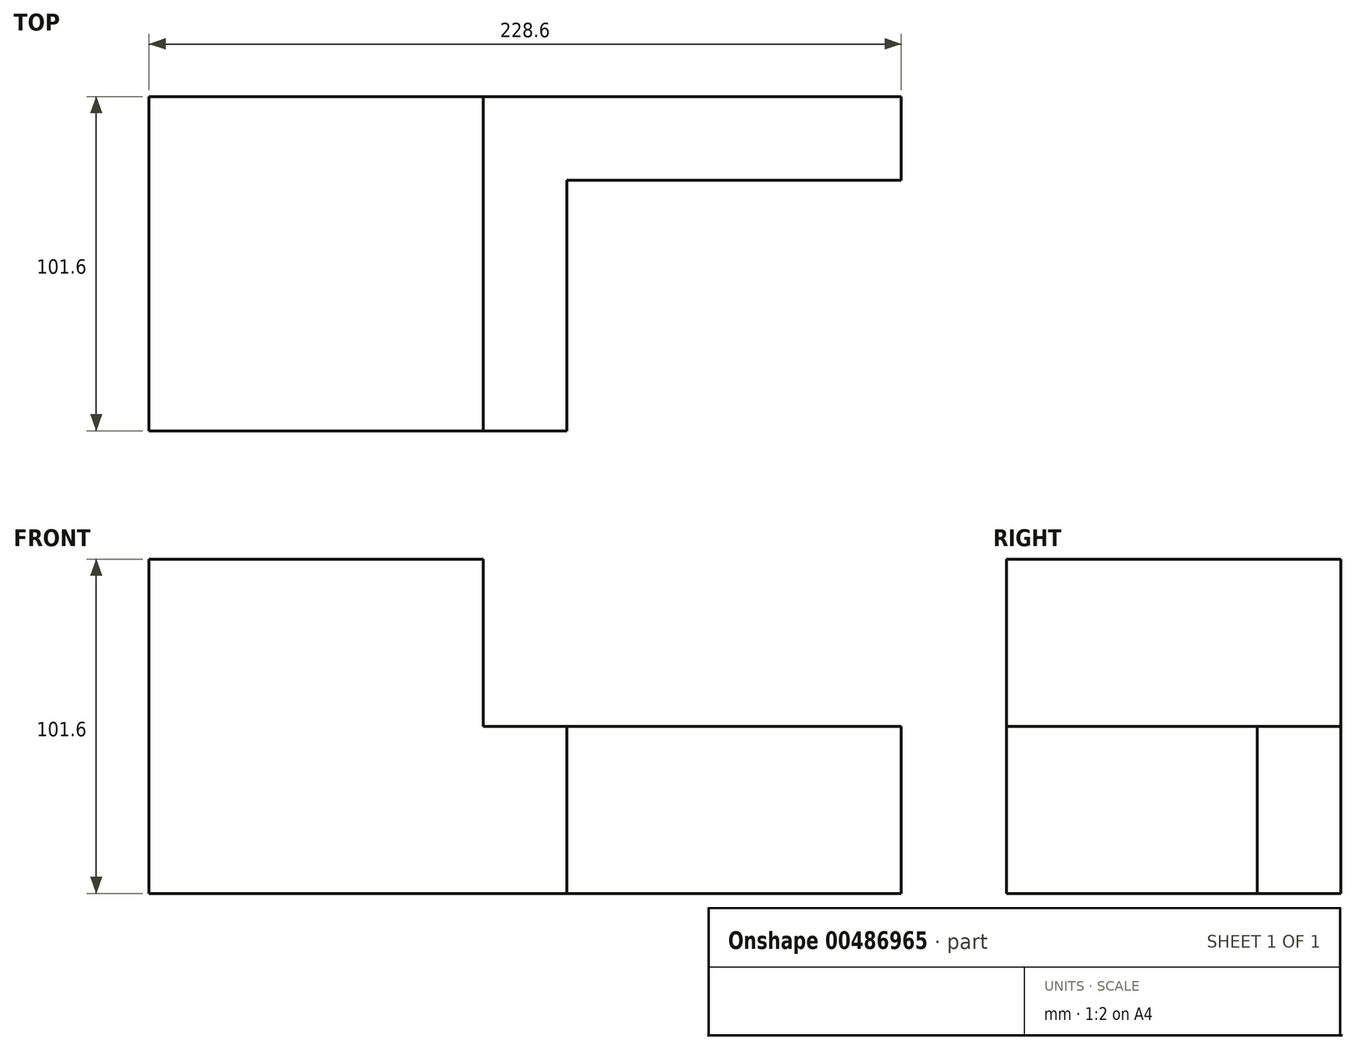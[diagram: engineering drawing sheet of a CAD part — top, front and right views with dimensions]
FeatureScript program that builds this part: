
annotation { "Feature Type Name" : "Feature", "Feature Type Description" : "" }
export const myFeature = defineFeature(function(context is Context, id is Id, definition is map)
    precondition{}
    {
        {
            var Q0;
            Q0=qCreatedBy(makeId("Front.planeOp"),FACE);
            var sketch = newSketch(context, id + "F0", { "sketchPlane" : qUnion([Q0])});
            skLineSegment(sketch, "E0.bottom", {"start": v(0, 0) * mm, "end": v(127, 0) * mm});
            skLineSegment(sketch, "E0.top", {"start": v(0, 50.8) * mm, "end": v(127, 50.8) * mm});
            skLineSegment(sketch, "E0.left", {"start": v(0, 0) * mm, "end": v(0, 50.8) * mm});
            skLineSegment(sketch, "E0.right", {"start": v(127, 0) * mm, "end": v(127, 50.8) * mm});
            skLineSegment(sketch, "E1.bottom", {"start": v(0, 0) * mm, "end": v(-101.6, 0) * mm});
            skLineSegment(sketch, "E1.top", {"start": v(0, 101.6) * mm, "end": v(-101.6, 101.6) * mm});
            skLineSegment(sketch, "E1.left", {"start": v(0, 0) * mm, "end": v(0, 101.6) * mm});
            skLineSegment(sketch, "E1.right", {"start": v(-101.6, 0) * mm, "end": v(-101.6, 101.6) * mm});
            skSolve(sketch);
        }
        {
            var Q0;
            {var subQ3=sQuery(id+"F0.wireOp",EDGE,"E1.bottom");Q0=makeQuery(id+"F0.imprint","IMPRINT",FACE,{"disambiguationData":[TD([[makeQuery(id+"F0.imprint","IMPRINT",EDGE,{"derivedFrom":subQ3}),-1.0]])]});}
            var Q1;
            {var subQ0=sQuery(id+"F0.wireOp",EDGE,"E0.bottom");Q1=makeQuery(id+"F0.imprint","IMPRINT",FACE,{"disambiguationData":[TD([[makeQuery(id+"F0.imprint","IMPRINT",EDGE,{"derivedFrom":subQ0}),1.0]])]});}
            extrude(context, id + "F1", {"entities" : qUnion([Q0, Q1]), "depth" : 101.6 * mm});
        }
        {
            var Q0;
            Q0=makeQuery(id+"F1.opExtrude","SWEPT_FACE",FACE,{"disambiguationData":[OSD([sQuery(id+"F0.wireOp",EDGE,"E0.top")])]});
            var sketch = newSketch(context, id + "F2", { "sketchPlane" : qUnion([Q0])});
            skLineSegment(sketch, "E2.bottom", {"start": v(127, -101.6) * mm, "end": v(25.4, -101.6) * mm});
            skLineSegment(sketch, "E2.top", {"start": v(127, -25.4) * mm, "end": v(25.4, -25.4) * mm});
            skLineSegment(sketch, "E2.left", {"start": v(127, -101.6) * mm, "end": v(127, -25.4) * mm});
            skLineSegment(sketch, "E2.right", {"start": v(25.4, -101.6) * mm, "end": v(25.4, -25.4) * mm});
            skSolve(sketch);
        }
        {
            var Q0;
            Q0=makeQuery(id+"F2.imprint","IMPRINT",FACE,{"disambiguationData":[TD([[makeQuery(id+"F2.imprint","IMPRINT",EDGE,{"derivedFrom":sQuery(id+"F2.wireOp",EDGE,"E2.bottom")}),1.0]])]});
            extrude(context, id + "F3", {"entities" : qUnion([Q0]), "operationType" : NewBodyOperationType.REMOVE, "oppositeDirection" : true, "depth" : 50.8 * mm});
        }
    });
